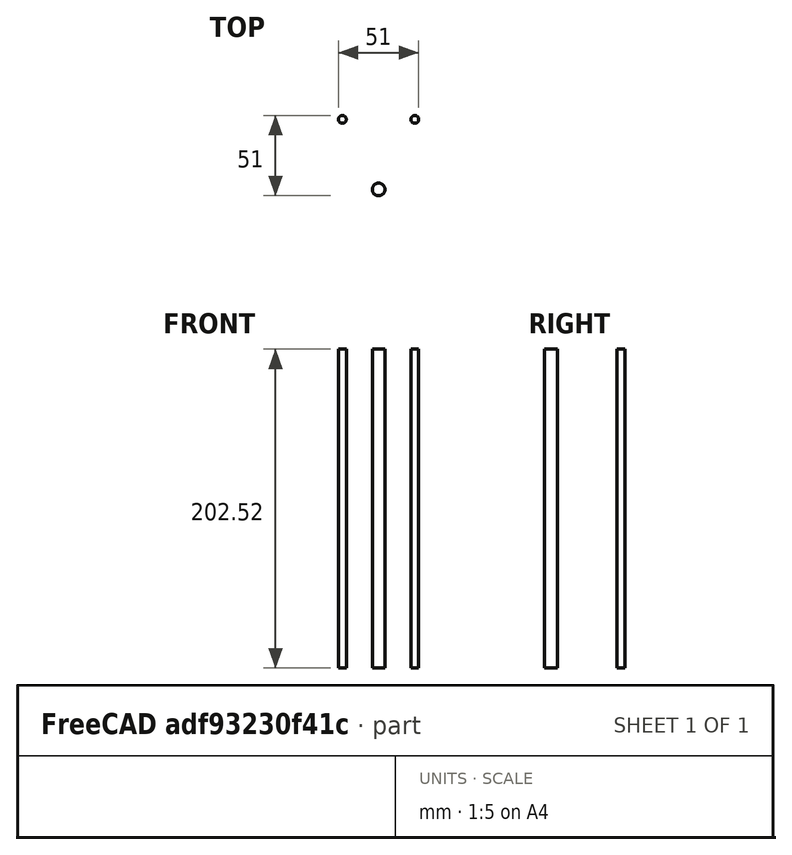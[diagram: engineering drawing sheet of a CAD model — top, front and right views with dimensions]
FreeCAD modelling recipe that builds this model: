
FCSTD DOCUMENT  (FreeCAD 0.20R29177 (Git))
Label: Stator_CoilWinder_Pins_Triangular
License: All rights reserved
LicenseURL: http://en.wikipedia.org/wiki/All_rights_reserved
objects: PartDesign::SubShapeBinder×1, Part::Extrusion×1, Spreadsheet::Sheet×1
note: 2 computed .brp shape members not serialized (recipe doc carries the construction recipe); baked Part::Feature solids carry a one-line shape summary decoded from their .brp
EXTERNAL_REF file=Stator_CoilWinder_Cheek_Triangular.FCStd obj=PolarPattern001Body
EXTERNAL_REF file=../../../Master_of_Puppets.FCStd obj=Alternator

FEATURE [PartDesign::SubShapeBinder] Binder  label="HolesSketchBinder"
  BindCopyOnChange = 0
  BindMode = 0
  ClaimChildren = false
  Fuse = false
  MakeFace = true
  OffsetFill = false
  OffsetIntersection = false
  OffsetJoinType = 0
  OffsetOpenResult = false
  PartialLoad = false
  Relative = true
  Support = -> [<external Stator_CoilWinder_Cheek_Triangular.FCStd>#PolarPattern001Body[Pocket001.Sketch006.]]
  _Version = 2
FEATURE [Part::Extrusion] Extrude  label="Stator_CoilWinder_Pins"
  Base = -> Binder
  Dir = (0,0,1)
  DirMode = 2
  FaceMakerClass = Part::FaceMakerBullseye
  LengthFwd = 202.52
  LengthRev = 0
  Solid = false
  Symmetric = false
  expr: LengthFwd = Spreadsheet.CoilWinderPinLength
FEATURE [Spreadsheet::Sheet] Spreadsheet
  cells = A1=Inputs; A2=CoilWinderPinLength; B2(CoilWinderPinLength)==Master_of_Puppets#Alternator.CoilWinderPinLength
